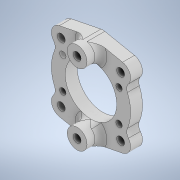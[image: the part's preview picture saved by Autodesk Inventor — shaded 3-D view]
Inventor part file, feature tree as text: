
AUTODESK INVENTOR PART (.ipt)
format: ipt  version: 2020 (Build 240168000, 168)  size: 408,064 bytes
history: native  units: mm
features: projected_geometry x9, sketch x8, extrude x6, other x3, hole x2, fillet x2, thicken_offset x2, plane x1, reference x1
ambient origin geometry x8: Origin, YZ Plane, XZ Plane, XY Plane, X Axis, Y Axis, Z Axis, Center Point
bodies: Solid1 (feature_tree)
feature tree (34):
  extrude  "Extrusion1"  Depth=20.0mm
  plane  "Work Plane1"
  extrude  "Extrusion3"  Depth=15.0mm
  hole  "Hole1"  [1 undecoded]
  fillet  "Fillet5"  Radius=5.0mm
  thicken_offset  "Thicken3"
  thicken_offset  "Thicken4"
  extrude  "Extrusion5"  Depth=4.0mm
  extrude  "Extrusion6"  Depth=1.0mm
  extrude  "Extrusion7"  Depth=1.0mm
  extrude  "Extrusion8"  Depth=4.0mm
  fillet  "Fillet7"  Radius=9.0mm
  hole  "Hole2"  [1 undecoded]
  sketch  "Sketch1"  dims[d0=13.0mm d1=20.0mm]
  reference  "Reference1"
  sketch  "Sketch3"  dims[d2=3.0mm d3=0.0mm d21=15.0mm]
  projected_geometry  "Projected Loop1"
  sketch  "Sketch4"  dims[d22=15.0mm d23=5.0mm d24=5.0mm]
  projected_geometry  "Projected Loop2"
  sketch  "Sketch6"  dims[d25=3.0mm d26=0.0mm]
  projected_geometry  "Projected Loop6"
  sketch  "Sketch7"  dims[d27=2.0mm d28=6.0mm d29=4.0mm d30=2.0mm d31=90.0deg d32=8.0mm d33=20.594885mm d34=2.0mm]
  projected_geometry  "Projected Loop7"
  sketch  "Sketch8"  dims[d35=1.0mm d36=1.0mm]
  projected_geometry  "Projected Loop8"
  sketch  "Sketch9"  dims[d37=1.0mm d38=1.0mm]
  projected_geometry  "Projected Loop9"
  sketch  "Sketch10"  dims[d61=9.0mm d62=5.0mm d63=9.0mm d64=5.0mm d65=10.0mm d66=0.0mm d67=10.0mm d68=0.0mm d69=10.0mm d70=0.0mm d71=5.0mm d72=5.0mm d73=3.5mm d74=0.0mm d75=1.5mm d76=2.0mm d77=6.0mm d78=4.0mm d79=2.0mm d80=90.0deg d81=20.0mm d82=0.0mm]
  projected_geometry  "Projected Loop10"
  projected_geometry  "Projected Loop11"
  projected_geometry  "Projected Loop12"
  other  "Assembly1"
  other  "brushless_20:1"
  other  "burshless_20_base:1"
note: 2 required parameter values undecoded (feature->parameter linkage not recoverable at this tier; creation-order binding heuristic only, values carry confidence <= 0.55)
